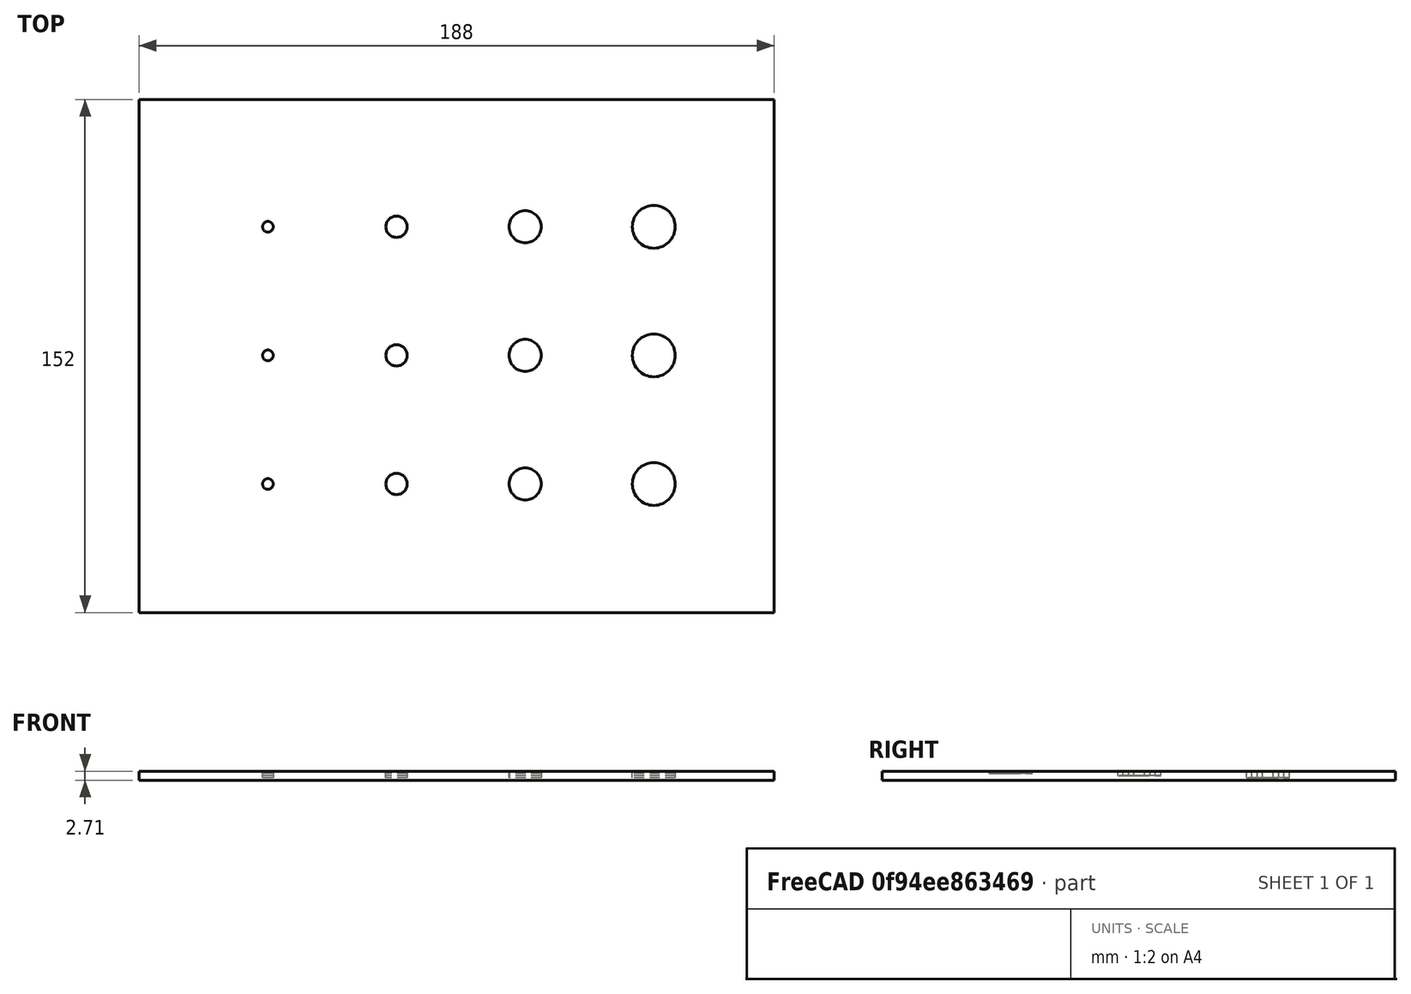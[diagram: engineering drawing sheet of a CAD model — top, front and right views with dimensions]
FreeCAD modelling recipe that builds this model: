
FCSTD DOCUMENT  (FreeCAD 0.16RUnknown)
Label: C16-NASAMODEL-FB1X
License: All rights reserved
LicenseURL: http://en.wikipedia.org/wiki/All_rights_reserved
objects: Sketcher::SketchObject×4, PartDesign::Pocket×3, Part::Extrusion×1, Mesh::Feature×1
note: 11 computed .brp shape members not serialized (recipe doc carries the construction recipe); baked Part::Feature solids carry a one-line shape summary decoded from their .brp

FEATURE [Sketcher::SketchObject] Sketch  label="FrontSide"
  sketch-geometry (4):
    g0: LineSegment StartX=0 StartY=0 StartZ=0 EndX=188 EndY=0 EndZ=0
    g1: LineSegment StartX=188 StartY=0 StartZ=0 EndX=188 EndY=152 EndZ=0
    g2: LineSegment StartX=188 StartY=152 StartZ=0 EndX=0 EndY=152 EndZ=0
    g3: LineSegment StartX=0 StartY=152 StartZ=0 EndX=0 EndY=0 EndZ=0
  constraints (11):
    c: Coincident(g3,g0)
    c: Coincident(g3,g2)
    c: Coincident(g2,g1)
    c: Coincident(g0,g1)
    c: Parallel(g0,g-1)
    c: Parallel(g3,g-2)
    c: Parallel(g0,g2)
    c: Parallel(g3,g1)
    c: Distance(g0) = 188  'length'
    c: Distance(g1) = 152
    c: Coincident(g0,g-1)
FEATURE [Part::Extrusion] Extrude
  Base = -> Sketch
  Dir = (0,0,2.71)
  Solid = true
FEATURE [Sketcher::SketchObject] Sketch003  label=".0765 holes"
  Placement = pos=(0,0,2.71) rot=(0,0,1;0rad)
  Support = -> Extrude [Face6]
  sketch-geometry (5):
    g0: Circle CenterX=38.1 CenterY=114.3 CenterZ=0 NormalX=0 NormalY=0 NormalZ=1 Radius=1.5875
    g1: Circle CenterX=76.2 CenterY=114.3 CenterZ=0 NormalX=0 NormalY=0 NormalZ=1 Radius=3.175
    g2: Circle CenterX=114.3 CenterY=114.3 CenterZ=0 NormalX=0 NormalY=0 NormalZ=1 Radius=4.7625
    g3: Circle CenterX=152.4 CenterY=114.3 CenterZ=0 NormalX=0 NormalY=0 NormalZ=1 Radius=6.35
    g4: LineSegment [constr] StartX=0 StartY=114.3 StartZ=0 EndX=152.4 EndY=114.3 EndZ=0
  constraints (16):
    c: DistanceY(g-1,g4) = 114.3
    c: PointOnObject(g0,g4)
    c: PointOnObject(g1,g4)
    c: PointOnObject(g2,g4)
    c: PointOnObject(g3,g4)
    c: PointOnObject(g4,g-2)
    c: Parallel(g4,g-1)
    c: DistanceX(g-2,g0) = 38.1
    c: DistanceX(g-2,g1) = 76.2
    c: DistanceX(g-2,g2) = 114.3
    c: DistanceX(g-2,g3) = 152.4
    c: Radius(g0) = 1.5875
    c: Radius(g1) = 3.175
    c: Radius(g2) = 4.7625
    c: Radius(g3) = 6.35
    c: Coincident(g4,g3)
FEATURE [PartDesign::Pocket] Pocket  label="Pocket .0765"
  Length = 1.9431
  Sketch = -> Sketch003
  Type = 0
FEATURE [Sketcher::SketchObject] Sketch002  label=".051 holes"
  Placement = pos=(0,0,2.71) rot=(0,0,1;0rad)
  Support = -> Pocket [Face5]
  sketch-geometry (5):
    g0: Circle CenterX=38.1 CenterY=76.2 CenterZ=0 NormalX=0 NormalY=0 NormalZ=1 Radius=1.5875
    g1: Circle CenterX=76.2 CenterY=76.2 CenterZ=0 NormalX=0 NormalY=0 NormalZ=1 Radius=3.175
    g2: Circle CenterX=114.3 CenterY=76.2 CenterZ=0 NormalX=0 NormalY=0 NormalZ=1 Radius=4.7625
    g3: Circle CenterX=152.4 CenterY=76.2 CenterZ=0 NormalX=0 NormalY=0 NormalZ=1 Radius=6.35
    g4: LineSegment [constr] StartX=0 StartY=76.2 StartZ=0 EndX=152.4 EndY=76.2 EndZ=0
  constraints (16):
    c: DistanceY(g-1,g4) = 76.2
    c: PointOnObject(g0,g4)
    c: PointOnObject(g1,g4)
    c: PointOnObject(g2,g4)
    c: PointOnObject(g3,g4)
    c: PointOnObject(g4,g-2)
    c: Parallel(g4,g-1)
    c: DistanceX(g-2,g0) = 38.1
    c: DistanceX(g-2,g1) = 76.2
    c: DistanceX(g-2,g2) = 114.3
    c: DistanceX(g-2,g3) = 152.4
    c: Radius(g0) = 1.5875
    c: Radius(g1) = 3.175
    c: Radius(g2) = 4.7625
    c: Radius(g3) = 6.35
    c: Coincident(g4,g3)
FEATURE [PartDesign::Pocket] Pocket001  label="Pocket .051"
  Length = 1.2954
  Sketch = -> Sketch002
  Type = 0
FEATURE [Sketcher::SketchObject] Sketch001  label=".0255 holes"
  Placement = pos=(0,0,2.71) rot=(0,0,1;0rad)
  Support = -> Pocket001 [Face5]
  sketch-geometry (5):
    g0: Circle CenterX=38.1 CenterY=38.1 CenterZ=0 NormalX=0 NormalY=0 NormalZ=1 Radius=1.5875
    g1: Circle CenterX=76.2 CenterY=38.1 CenterZ=0 NormalX=0 NormalY=0 NormalZ=1 Radius=3.175
    g2: Circle CenterX=114.3 CenterY=38.1 CenterZ=0 NormalX=0 NormalY=0 NormalZ=1 Radius=4.7625
    g3: Circle CenterX=152.4 CenterY=38.1 CenterZ=0 NormalX=0 NormalY=0 NormalZ=1 Radius=6.35
    g4: LineSegment [constr] StartX=0 StartY=38.1 StartZ=0 EndX=152.4 EndY=38.1 EndZ=0
  constraints (16):
    c: DistanceY(g-1,g4) = 38.1
    c: PointOnObject(g0,g4)
    c: PointOnObject(g1,g4)
    c: PointOnObject(g2,g4)
    c: PointOnObject(g3,g4)
    c: PointOnObject(g4,g-2)
    c: Parallel(g4,g-1)
    c: DistanceX(g-2,g0) = 38.1
    c: DistanceX(g-2,g1) = 76.2
    c: DistanceX(g-2,g2) = 114.3
    c: DistanceX(g-2,g3) = 152.4
    c: Radius(g0) = 1.5875
    c: Radius(g1) = 3.175
    c: Radius(g2) = 4.7625
    c: Radius(g3) = 6.35
    c: Coincident(g4,g3)
FEATURE [PartDesign::Pocket] Pocket002  label="Pocket .0255"
  Length = 0.6477
  Sketch = -> Sketch001
  Type = 0
FEATURE [Mesh::Feature] Mesh  label="Pocket .0255 (Meshed)"
